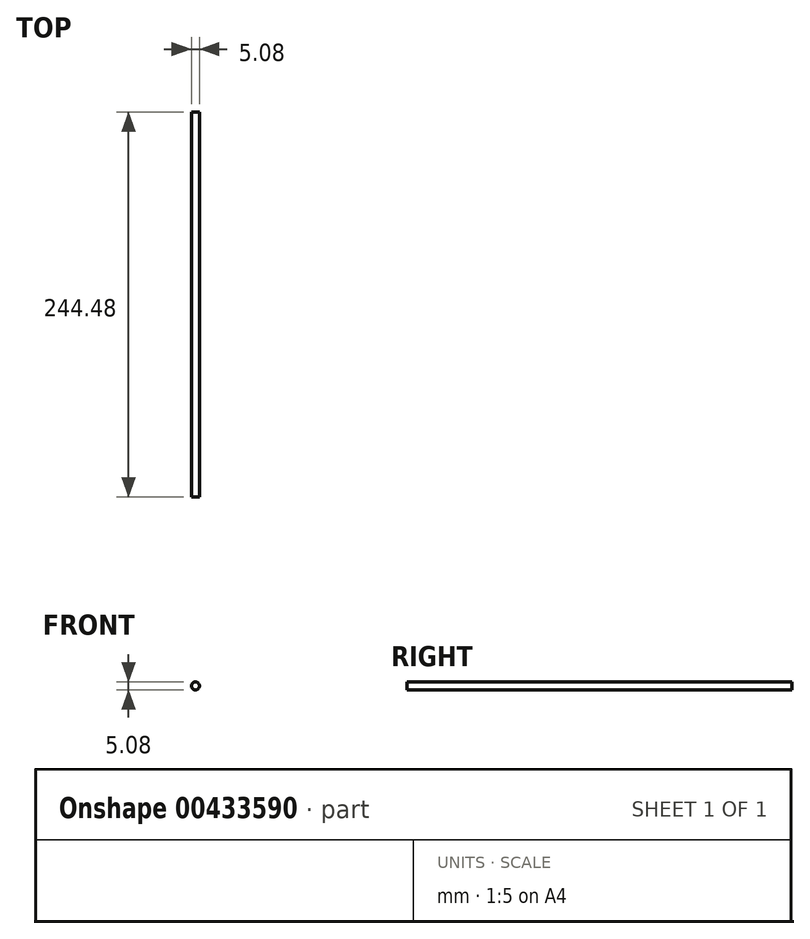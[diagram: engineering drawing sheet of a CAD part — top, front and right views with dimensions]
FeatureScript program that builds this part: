
annotation { "Feature Type Name" : "Feature", "Feature Type Description" : "" }
export const myFeature = defineFeature(function(context is Context, id is Id, definition is map)
    precondition{}
    {
        {
            var Q0;
            Q0=qCreatedBy(makeId("Front.planeOp"),FACE);
            var sketch = newSketch(context, id + "F0", { "sketchPlane" : qUnion([Q0])});
            skCircle(sketch, "E0", {"center": v(0, 0) * mm, "radius": 2.54 * mm});
            skSolve(sketch);
        }
        {
            var Q0;
            Q0=makeQuery(id+"F0.imprint","IMPRINT",FACE,{"disambiguationData":[TD([[makeQuery(id+"F0.imprint","IMPRINT",EDGE,{"derivedFrom":sQuery(id+"F0.wireOp",EDGE,"E0")}),1.0]])]});
            extrude(context, id + "F1", {"entities" : qUnion([Q0]), "depth" : 244.47 * mm});
        }
    });
